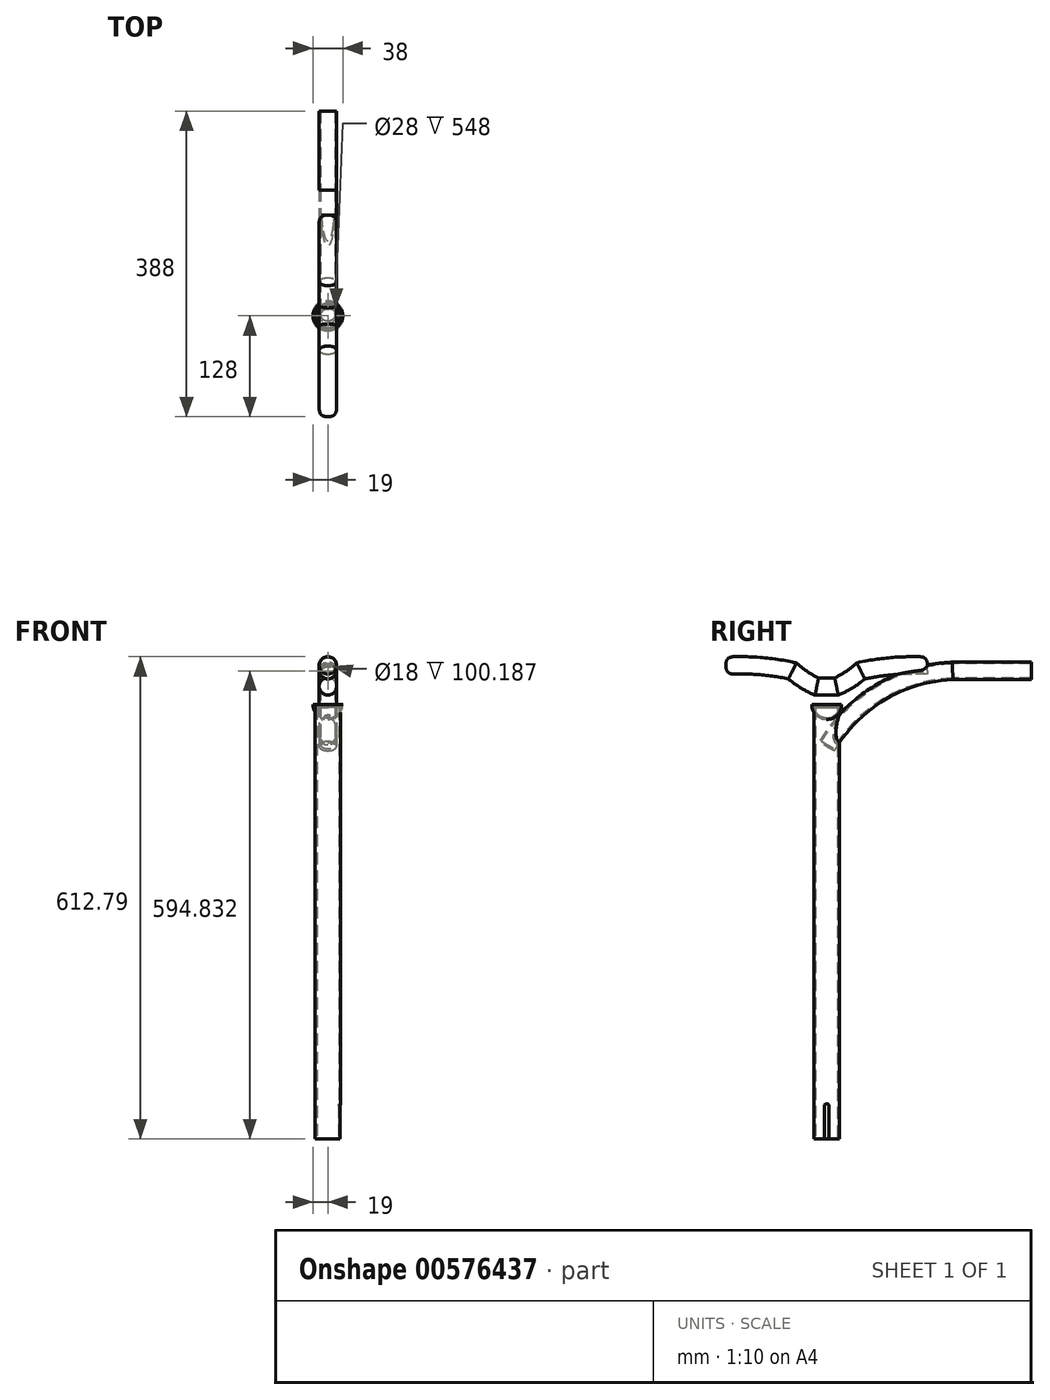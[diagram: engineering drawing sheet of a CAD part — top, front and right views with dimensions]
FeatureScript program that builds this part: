
annotation { "Feature Type Name" : "Feature", "Feature Type Description" : "" }
export const myFeature = defineFeature(function(context is Context, id is Id, definition is map)
    precondition{}
    {
        {
            var Q0;
            Q0=qCreatedBy(makeId("Top.planeOp"),FACE);
            var sketch = newSketch(context, id + "F0", { "sketchPlane" : qUnion([Q0])});
            skCircle(sketch, "E0", {"center": v(0, 0) * mm, "radius": 16 * mm});
            skSolve(sketch);
        }
        {
            var Q0;
            Q0 = qSketchRegion(id + "F0", true);
            extrude(context, id + "F1", {"entities" : qUnion([Q0]), "depth" : 550 * mm, "offsetDistance" : 25 * mm});
        }
        {
            var Q0;
            Q0=makeQuery(id+"F1.opExtrude","CAP_FACE",FACE,{"disambiguationData":[OSD([sQuery(id+"F0.wireOp",EDGE,"E0")])],"isStart":true});
            shell(context, id + "F2", {"entities" : qUnion([Q0]), "thickness" : 2 * mm});
        }
        {
            var Q0;
            Q0=qCreatedBy(makeId("Right.planeOp"),FACE);
            var sketch = newSketch(context, id + "F3", { "sketchPlane" : qUnion([Q0])});
            skLineSegment(sketch, "E1.bottom", {"start": v(-3, 0) * mm, "end": v(3, 0) * mm});
            skLineSegment(sketch, "E1.top", {"start": v(0, 45) * mm, "end": v(0, 45) * mm});
            skLineSegment(sketch, "E1.left", {"start": v(-3, 0) * mm, "end": v(-3, 42) * mm});
            skLineSegment(sketch, "E1.right", {"start": v(3, 0) * mm, "end": v(3, 42) * mm});
            skPoint(sketch, "E2.visualSharp", {"position": v(-3, 45) * mm});
            skArc(sketch, "E2.filletArc", {"start": v(0, 45) * mm, "mid": v(-2.12, 44.12) * mm, "end": v(-3, 42) * mm});
            skPoint(sketch, "E3.visualSharp", {"position": v(3, 45) * mm});
            skArc(sketch, "E3.filletArc", {"start": v(3, 42) * mm, "mid": v(2.12, 44.12) * mm, "end": v(0, 45) * mm});
            skSolve(sketch);
        }
        {
            var Q0;
            Q0 = qSketchRegion(id + "F3", true);
            extrude(context, id + "F4", {"entities" : qUnion([Q0]), "operationType" : NewBodyOperationType.REMOVE, "endBound" : BoundingType.THROUGH_ALL, "depth" : 25 * mm, "offsetDistance" : 25 * mm});
        }
        {
            var Q0;
            Q0=qCreatedBy(makeId("Right.planeOp"),FACE);
            var sketch = newSketch(context, id + "F5", { "sketchPlane" : qUnion([Q0])});
            skArc(sketch, "E4", {"start": v(160, 594.83) * mm, "mid": v(67.78, 567.22) * mm, "end": v(0, 498.86) * mm});
            skLineSegment(sketch, "E5", {"start": v(160, 594.83) * mm, "end": v(260, 594.83) * mm});
            skSolve(sketch);
        }
        {
            var Q0;
            Q0=qCreatedBy(makeId("Front.planeOp"),FACE);
            var Q1;
            Q1=sQuery(id+"F5.wireOp",VERTEX,"E5.end");
            cPlane(context, id + "F6", {"entities" : qUnion([Q0, Q1]), "cplaneType" : CPlaneType.PLANE_POINT, "offset" : 25 * mm, "width" : 150 * mm, "height" : 150 * mm});
        }
        {
            var Q0;
            Q0=qCreatedBy(id+"F6.planeOp",FACE);
            var sketch = newSketch(context, id + "F7", { "sketchPlane" : qUnion([Q0])});
            skCircle(sketch, "E6", {"center": v(0, 594.83) * mm, "radius": 11 * mm});
            skSolve(sketch);
        }
        {
            var Q0;
            Q0 = qSketchRegion(id + "F7", true);
            var Q1;
            Q1 = qConstructionFilter(qBodyType(qCreatedBy(id + "F5" ,EDGE), BodyType.WIRE), ConstructionObject.NO);
            sweep(context, id + "F8", {"operationType" : NewBodyOperationType.ADD, "profiles" : qUnion([Q0]), "path" : qUnion([Q1])});
        }
        {
            var Q0;
            Q0=makeQuery(id+"F8.opSweep","CAP_FACE",FACE,{"disambiguationData":[OSD([sQuery(id+"F5.wireOp",VERTEX,"E5.end"),sQuery(id+"F7.wireOp",EDGE,"E6")])],"isStart":true});
            shell(context, id + "F9", {"entities" : qUnion([Q0]), "thickness" : 2 * mm});
        }
        {
            var Q0;
            Q0=qCreatedBy(makeId("Right.planeOp"),FACE);
            var sketch = newSketch(context, id + "F10", { "sketchPlane" : qUnion([Q0])});
            skLineSegment(sketch, "E7", {"start": v(-128, 601.8) * mm, "end": v(-108, 601.8) * mm});
            skArc(sketch, "E8", {"start": v(-43.42, 594.78) * mm, "mid": v(-75.52, 600.03) * mm, "end": v(-108, 601.8) * mm});
            skArc(sketch, "E9", {"start": v(-43.42, 594.78) * mm, "mid": v(-28.77, 583.62) * mm, "end": v(-12.5, 575) * mm});
            skLineSegment(sketch, "E10", {"start": v(-12.5, 575) * mm, "end": v(0, 575) * mm});
            skLineSegment(sketch, "E11.MirrorCS", {"start": v(12.5, 575) * mm, "end": v(0, 575) * mm});
            skArc(sketch, "E12.MirrorCS", {"start": v(43.42, 594.78) * mm, "mid": v(28.77, 583.62) * mm, "end": v(12.5, 575) * mm});
            skArc(sketch, "E13.MirrorCS", {"start": v(43.42, 594.78) * mm, "mid": v(75.52, 600.03) * mm, "end": v(108, 601.8) * mm});
            skLineSegment(sketch, "E14.MirrorCS", {"start": v(128, 601.8) * mm, "end": v(108, 601.8) * mm});
            skSolve(sketch);
        }
        {
            var Q0;
            Q0=sQuery(id+"F10.wireOp",VERTEX,"E14.MirrorCS.start");
            var Q1;
            Q1=qCreatedBy(id+"F6.planeOp",FACE);
            cPlane(context, id + "F11", {"entities" : qUnion([Q0, Q1]), "cplaneType" : CPlaneType.PLANE_POINT, "offset" : 25 * mm, "width" : 150 * mm, "height" : 150 * mm});
        }
        {
            var Q0;
            Q0=qCreatedBy(id+"F11.planeOp",FACE);
            var sketch = newSketch(context, id + "F12", { "sketchPlane" : qUnion([Q0])});
            skCircle(sketch, "E15", {"center": v(0, 601.8) * mm, "radius": 11 * mm});
            skSolve(sketch);
        }
        {
            var Q0;
            Q0 = qSketchRegion(id + "F12", true);
            var Q1;
            Q1 = qConstructionFilter(qBodyType(qCreatedBy(id + "F10" ,EDGE), BodyType.WIRE), ConstructionObject.NO);
            sweep(context, id + "F13", {"operationType" : NewBodyOperationType.ADD, "profiles" : qUnion([Q0]), "path" : qUnion([Q1])});
        }
        {
            var Q0;
            Q0=makeQuery(id+"F13.opSweep","CAP_EDGE",EDGE,{"disambiguationData":[OSD([sQuery(id+"F10.wireOp",VERTEX,"E7.start"),sQuery(id+"F12.wireOp",EDGE,"E15")])],"isStart":false});
            var Q1;
            {var subQ0=sQuery(id+"F12.wireOp",EDGE,"E15");var subQ1=sQuery(id+"F10.wireOp",VERTEX,"E14.MirrorCS.start");Q1=makeQuery(id+"F13.boolean.opBoolean","SPLIT",EDGE,{"disambiguationData":[TD([makeQuery(id+"F8.opSweep","SWEPT_FACE",FACE,{"disambiguationData":[OSD([sQuery(id+"F5.wireOp",EDGE,"E4"),sQuery(id+"F7.wireOp",EDGE,"E6")])]})])],"derivedFrom":makeQuery(id+"F13.opSweep","CAP_EDGE",EDGE,{"disambiguationData":[OSD([subQ1,subQ0])],"isStart":true})});}
            fillet(context, id + "F14", {"entities" : qUnion([Q0, Q1]), "radius" : 10 * mm, "tangentPropagation" : true, "rho" : 0.5, "crossSection" : FilletCrossSection.CONIC, "allowEdgeOverflow" : false});
        }
        {
            var Q0;
            Q0=qCreatedBy(makeId("Right.planeOp"),FACE);
            var sketch = newSketch(context, id + "F15", { "sketchPlane" : qUnion([Q0])});
            skArc(sketch, "E16", {"start": v(-19, 551.96) * mm, "mid": v(-13.42, 538.55) * mm, "end": v(0, 533) * mm});
            skLineSegment(sketch, "E17", {"start": v(0, 552) * mm, "end": v(0, 533) * mm});
            skLineSegment(sketch, "E18", {"start": v(-19, 551.96) * mm, "end": v(0, 551.98) * mm});
            skPoint(sketch, "E19.orphan", {"position": v(0, 571) * mm});
            skPoint(sketch, "E20.orphan", {"position": v(19, 552) * mm});
            skSolve(sketch);
        }
        {
            var Q0;
            Q0 = qSketchRegion(id + "F15", true);
            var Q1;
            Q1=sQuery(id+"F15.wireOp",EDGE,"E17");
            revolve(context, id + "F16", {"surfaceOperationType" : NewSurfaceOperationType.NEW, "entities" : qUnion([Q0]), "axis" : qUnion([Q1]), "revolveType" : RevolveType.FULL});
        }
        {
            var Q0;
            Q0=makeQuery(id+"F16.opRevolve","SWEPT_FACE",FACE,{"disambiguationData":[OSD([sQuery(id+"F15.wireOp",EDGE,"E18")])]});
            shell(context, id + "F17", {"entities" : qUnion([Q0]), "thickness" : 2 * mm});
        }
    });
